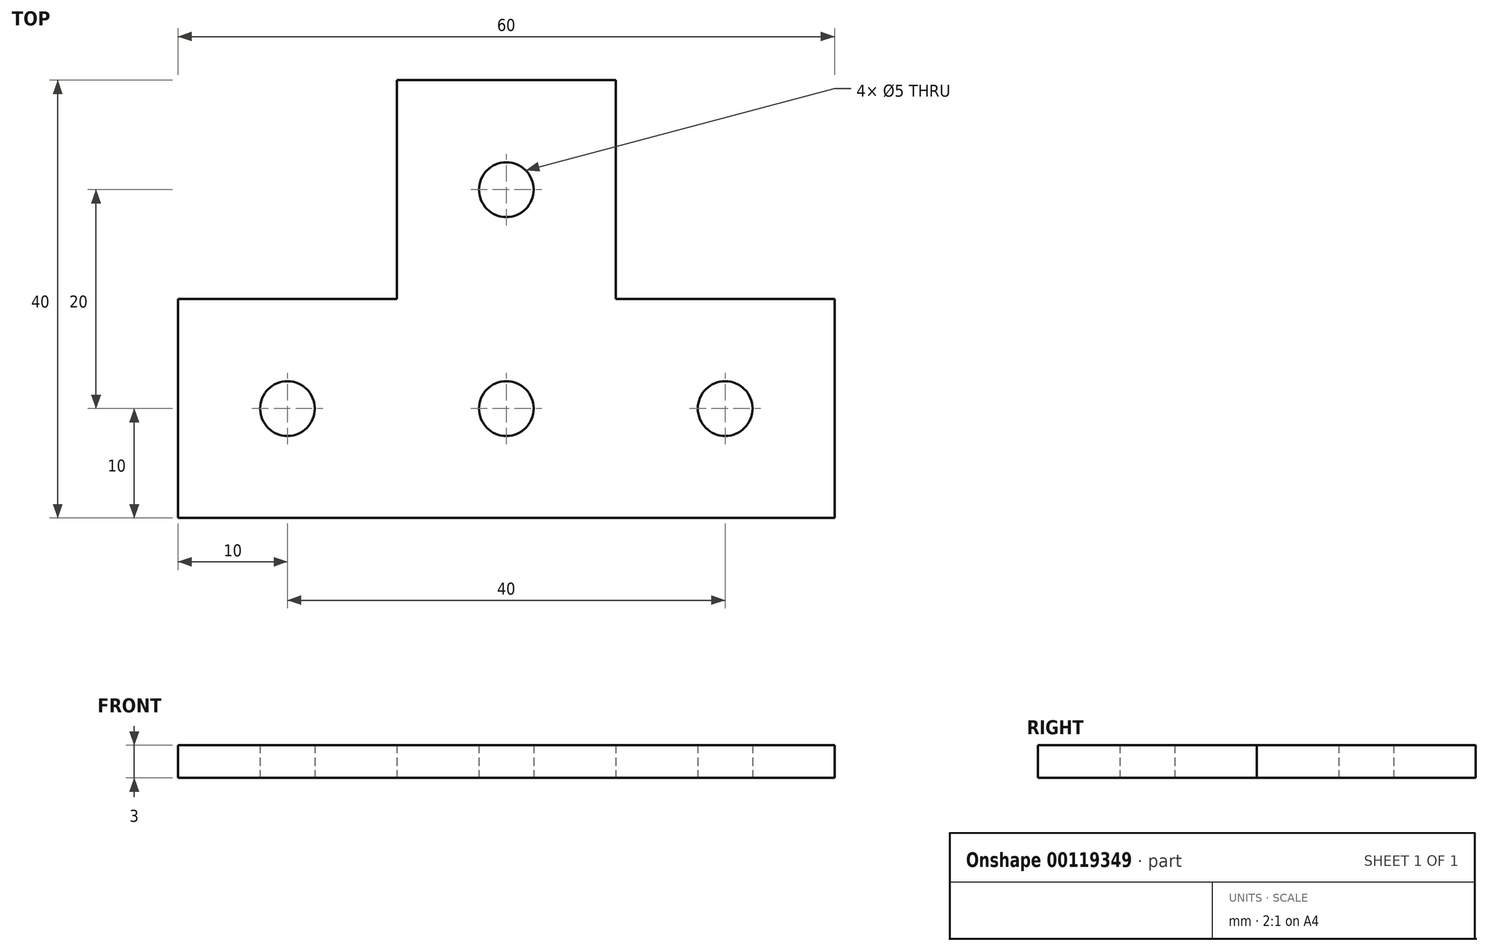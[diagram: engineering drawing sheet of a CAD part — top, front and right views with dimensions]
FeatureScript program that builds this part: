
annotation { "Feature Type Name" : "Feature", "Feature Type Description" : "" }
export const myFeature = defineFeature(function(context is Context, id is Id, definition is map)
    precondition{}
    {
        {
            var Q0;
            Q0=qCreatedBy(makeId("Top.planeOp"),FACE);
            var sketch = newSketch(context, id + "F0", { "sketchPlane" : qUnion([Q0])});
            skLineSegment(sketch, "E0", {"start": v(0, 0) * mm, "end": v(30, 0) * mm});
            skLineSegment(sketch, "E1", {"start": v(30, 0) * mm, "end": v(30, 20) * mm});
            skLineSegment(sketch, "E2", {"start": v(30, 20) * mm, "end": v(10, 20) * mm});
            skLineSegment(sketch, "E3", {"start": v(10, 20) * mm, "end": v(10, 40) * mm});
            skLineSegment(sketch, "E4", {"start": v(10, 40) * mm, "end": v(0, 40) * mm});
            skLineSegment(sketch, "E5.MirrorCS", {"start": v(-10, 40) * mm, "end": v(0, 40) * mm});
            skLineSegment(sketch, "E6.MirrorCS", {"start": v(-10, 20) * mm, "end": v(-10, 40) * mm});
            skLineSegment(sketch, "E7.MirrorCS", {"start": v(-30, 20) * mm, "end": v(-10, 20) * mm});
            skLineSegment(sketch, "E8.MirrorCS", {"start": v(-30, 0) * mm, "end": v(-30, 20) * mm});
            skLineSegment(sketch, "E9.MirrorCS", {"start": v(0, 0) * mm, "end": v(-30, 0) * mm});
            skLineSegment(sketch, "E10", {"start": v(-30, 10) * mm, "end": v(30, 10) * mm, "construction": true});
            skCircle(sketch, "E11", {"center": v(0, 30) * mm, "radius": 2.5 * mm});
            skCircle(sketch, "E12", {"center": v(-20, 10) * mm, "radius": 2.5 * mm});
            skCircle(sketch, "E13.MirrorC", {"center": v(20, 10) * mm, "radius": 2.5 * mm});
            skLineSegment(sketch, "E14", {"start": v(0, 30) * mm, "end": v(29.2, 30) * mm, "construction": true});
            skLineSegment(sketch, "E15", {"start": v(20, 10) * mm, "end": v(20, 15.79) * mm, "construction": true});
            skCircle(sketch, "E16", {"center": v(0, 10) * mm, "radius": 2.5 * mm});
            skSolve(sketch);
        }
        {
            var Q0;
            Q0 = qSketchRegion(id + "F0", true);
            extrude(context, id + "F1", {"entities" : qUnion([Q0]), "depth" : 3 * mm});
        }
    });
